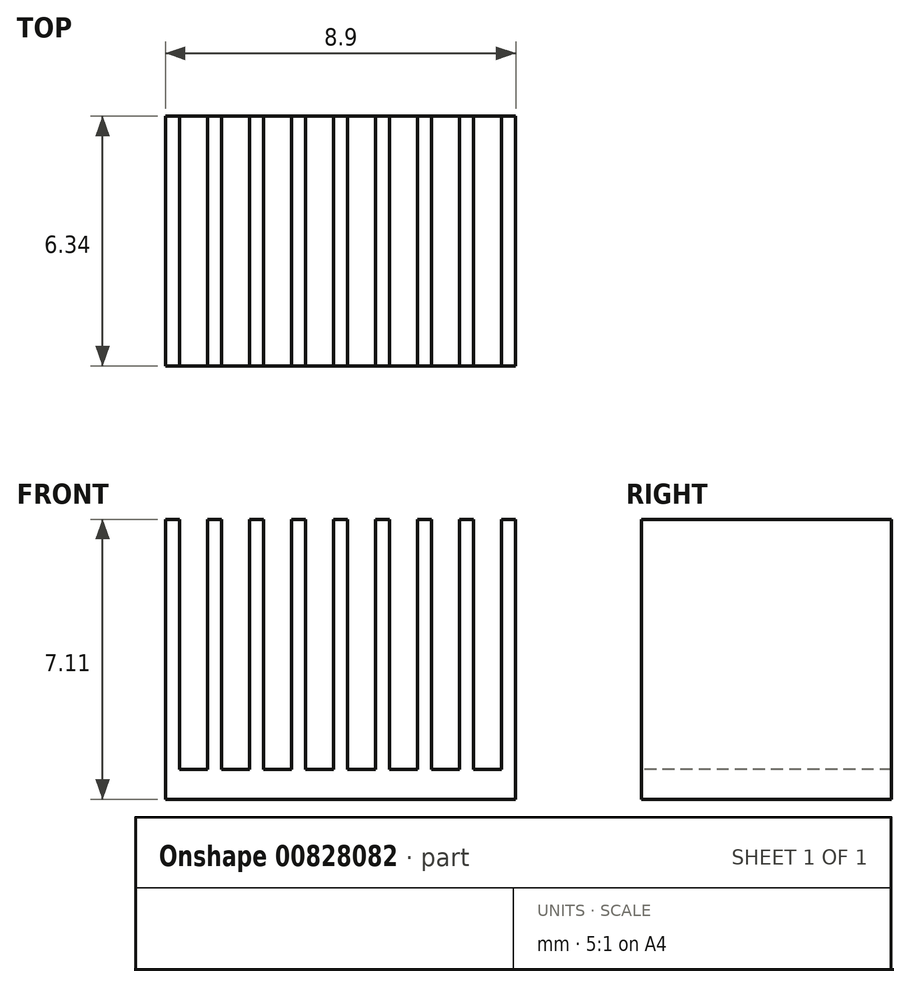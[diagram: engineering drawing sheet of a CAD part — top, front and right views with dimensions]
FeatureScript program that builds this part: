
annotation { "Feature Type Name" : "Feature", "Feature Type Description" : "" }
export const myFeature = defineFeature(function(context is Context, id is Id, definition is map)
    precondition{}
    {
        {
            var Q0;
            Q0=qCreatedBy(makeId("Top.planeOp"),FACE);
            var sketch = newSketch(context, id + "F0", { "sketchPlane" : qUnion([Q0])});
            skLineSegment(sketch, "E0.bottom", {"start": v(4.44, 3.18) * mm, "end": v(-4.45, 3.18) * mm});
            skLineSegment(sketch, "E0.top", {"start": v(4.45, -3.17) * mm, "end": v(-4.44, -3.17) * mm});
            skLineSegment(sketch, "E0.left", {"start": v(4.44, 3.18) * mm, "end": v(4.45, -3.17) * mm});
            skLineSegment(sketch, "E0.right", {"start": v(-4.45, 3.18) * mm, "end": v(-4.44, -3.17) * mm});
            skPoint(sketch, "E0.middle", {"position": v(0, 0) * mm});
            skSolve(sketch);
        }
        {
            var Q0;
            Q0=makeQuery(id+"F0.imprint","IMPRINT",FACE,{"disambiguationData":[TD([[makeQuery(id+"F0.imprint","IMPRINT",EDGE,{"derivedFrom":sQuery(id+"F0.wireOp",EDGE,"E0.bottom")}),1.0]])]});
            extrude(context, id + "F1", {"entities" : qUnion([Q0]), "depth" : 0.76 * mm, "offsetDistance" : 25.4 * mm});
        }
        {
            var Q0;
            Q0=makeQuery(id+"F1.opExtrude","CAP_FACE",FACE,{"disambiguationData":[OSD([sQuery(id+"F0.wireOp",EDGE,"E0.bottom"),sQuery(id+"F0.wireOp",EDGE,"E0.top"),sQuery(id+"F0.wireOp",EDGE,"E0.left"),sQuery(id+"F0.wireOp",EDGE,"E0.right")])],"isStart":false});
            var sketch = newSketch(context, id + "F2", { "sketchPlane" : qUnion([Q0])});
            skLineSegment(sketch, "E1.bottom", {"start": v(-4.45, 3.18) * mm, "end": v(-4.09, 3.18) * mm});
            skLineSegment(sketch, "E1.top", {"start": v(-4.45, -3.17) * mm, "end": v(-4.09, -3.17) * mm});
            skLineSegment(sketch, "E1.left", {"start": v(-4.45, 3.18) * mm, "end": v(-4.45, -3.17) * mm});
            skLineSegment(sketch, "E1.right", {"start": v(-4.09, 3.18) * mm, "end": v(-4.09, -3.17) * mm});
            skLineSegment(sketch, "E2.1.0.0", {"start": v(-3.02, 3.18) * mm, "end": v(-3.02, -3.17) * mm});
            skLineSegment(sketch, "E2.1.0.1", {"start": v(-3.38, 3.18) * mm, "end": v(-3.02, 3.18) * mm});
            skLineSegment(sketch, "E2.1.0.2", {"start": v(-3.38, 3.18) * mm, "end": v(-3.38, -3.17) * mm});
            skLineSegment(sketch, "E2.1.0.3", {"start": v(-3.38, -3.17) * mm, "end": v(-3.02, -3.17) * mm});
            skLineSegment(sketch, "E2.2.0.0", {"start": v(-1.96, 3.18) * mm, "end": v(-1.96, -3.17) * mm});
            skLineSegment(sketch, "E2.2.0.1", {"start": v(-2.31, 3.18) * mm, "end": v(-1.96, 3.18) * mm});
            skLineSegment(sketch, "E2.2.0.2", {"start": v(-2.31, 3.18) * mm, "end": v(-2.31, -3.17) * mm});
            skLineSegment(sketch, "E2.2.0.3", {"start": v(-2.31, -3.17) * mm, "end": v(-1.96, -3.17) * mm});
            skLineSegment(sketch, "E2.3.0.0", {"start": v(-0.89, 3.18) * mm, "end": v(-0.89, -3.17) * mm});
            skLineSegment(sketch, "E2.3.0.1", {"start": v(-1.24, 3.18) * mm, "end": v(-0.89, 3.18) * mm});
            skLineSegment(sketch, "E2.3.0.2", {"start": v(-1.24, 3.18) * mm, "end": v(-1.24, -3.17) * mm});
            skLineSegment(sketch, "E2.3.0.3", {"start": v(-1.24, -3.17) * mm, "end": v(-0.89, -3.17) * mm});
            skLineSegment(sketch, "E2.4.0.0", {"start": v(0.18, 3.18) * mm, "end": v(0.18, -3.17) * mm});
            skLineSegment(sketch, "E2.4.0.1", {"start": v(-0.18, 3.18) * mm, "end": v(0.18, 3.18) * mm});
            skLineSegment(sketch, "E2.4.0.2", {"start": v(-0.18, 3.18) * mm, "end": v(-0.18, -3.17) * mm});
            skLineSegment(sketch, "E2.4.0.3", {"start": v(-0.18, -3.17) * mm, "end": v(0.18, -3.17) * mm});
            skLineSegment(sketch, "E2.5.0.0", {"start": v(1.24, 3.18) * mm, "end": v(1.24, -3.17) * mm});
            skLineSegment(sketch, "E2.5.0.1", {"start": v(0.89, 3.18) * mm, "end": v(1.24, 3.18) * mm});
            skLineSegment(sketch, "E2.5.0.2", {"start": v(0.89, 3.18) * mm, "end": v(0.89, -3.17) * mm});
            skLineSegment(sketch, "E2.5.0.3", {"start": v(0.89, -3.17) * mm, "end": v(1.24, -3.17) * mm});
            skLineSegment(sketch, "E2.6.0.0", {"start": v(2.31, 3.18) * mm, "end": v(2.31, -3.17) * mm});
            skLineSegment(sketch, "E2.6.0.1", {"start": v(1.96, 3.18) * mm, "end": v(2.31, 3.18) * mm});
            skLineSegment(sketch, "E2.6.0.2", {"start": v(1.96, 3.18) * mm, "end": v(1.96, -3.17) * mm});
            skLineSegment(sketch, "E2.6.0.3", {"start": v(1.96, -3.17) * mm, "end": v(2.31, -3.17) * mm});
            skLineSegment(sketch, "E2.7.0.0", {"start": v(3.38, 3.18) * mm, "end": v(3.38, -3.17) * mm});
            skLineSegment(sketch, "E2.7.0.1", {"start": v(3.02, 3.18) * mm, "end": v(3.38, 3.18) * mm});
            skLineSegment(sketch, "E2.7.0.2", {"start": v(3.02, 3.18) * mm, "end": v(3.02, -3.17) * mm});
            skLineSegment(sketch, "E2.7.0.3", {"start": v(3.02, -3.17) * mm, "end": v(3.38, -3.17) * mm});
            skLineSegment(sketch, "E2.8.0.0", {"start": v(4.44, 3.18) * mm, "end": v(4.44, -3.17) * mm});
            skLineSegment(sketch, "E2.8.0.1", {"start": v(4.09, 3.18) * mm, "end": v(4.44, 3.18) * mm});
            skLineSegment(sketch, "E2.8.0.2", {"start": v(4.09, 3.18) * mm, "end": v(4.09, -3.17) * mm});
            skLineSegment(sketch, "E2.8.0.3", {"start": v(4.09, -3.17) * mm, "end": v(4.44, -3.17) * mm});
            skLineSegment(sketch, "E2.direction1", {"start": v(-4.09, -3.17) * mm, "end": v(-3.02, -3.17) * mm, "construction": true});
            skSolve(sketch);
        }
        {
            var Q0;
            Q0=makeQuery(id+"F2.imprint","IMPRINT",FACE,{"disambiguationData":[TD([[makeQuery(id+"F2.imprint","IMPRINT",EDGE,{"derivedFrom":sQuery(id+"F2.wireOp",EDGE,"E1.bottom")}),1.0]])]});
            var Q1;
            Q1=makeQuery(id+"F2.imprint","IMPRINT",FACE,{"disambiguationData":[TD([[makeQuery(id+"F2.imprint","IMPRINT",EDGE,{"derivedFrom":sQuery(id+"F2.wireOp",EDGE,"E2.1.0.0")}),-1.0]])]});
            var Q2;
            Q2=makeQuery(id+"F2.imprint","IMPRINT",FACE,{"disambiguationData":[TD([[makeQuery(id+"F2.imprint","IMPRINT",EDGE,{"derivedFrom":sQuery(id+"F2.wireOp",EDGE,"E2.2.0.0")}),-1.0]])]});
            var Q3;
            Q3=makeQuery(id+"F2.imprint","IMPRINT",FACE,{"disambiguationData":[TD([[makeQuery(id+"F2.imprint","IMPRINT",EDGE,{"derivedFrom":sQuery(id+"F2.wireOp",EDGE,"E2.3.0.0")}),-1.0]])]});
            var Q4;
            Q4=makeQuery(id+"F2.imprint","IMPRINT",FACE,{"disambiguationData":[TD([[makeQuery(id+"F2.imprint","IMPRINT",EDGE,{"derivedFrom":sQuery(id+"F2.wireOp",EDGE,"E2.4.0.0")}),-1.0]])]});
            var Q5;
            Q5=makeQuery(id+"F2.imprint","IMPRINT",FACE,{"disambiguationData":[TD([[makeQuery(id+"F2.imprint","IMPRINT",EDGE,{"derivedFrom":sQuery(id+"F2.wireOp",EDGE,"E2.5.0.0")}),-1.0]])]});
            var Q6;
            Q6=makeQuery(id+"F2.imprint","IMPRINT",FACE,{"disambiguationData":[TD([[makeQuery(id+"F2.imprint","IMPRINT",EDGE,{"derivedFrom":sQuery(id+"F2.wireOp",EDGE,"E2.6.0.0")}),-1.0]])]});
            var Q7;
            Q7=makeQuery(id+"F2.imprint","IMPRINT",FACE,{"disambiguationData":[TD([[makeQuery(id+"F2.imprint","IMPRINT",EDGE,{"derivedFrom":sQuery(id+"F2.wireOp",EDGE,"E2.7.0.0")}),-1.0]])]});
            var Q8;
            Q8=makeQuery(id+"F2.imprint","IMPRINT",FACE,{"disambiguationData":[TD([[makeQuery(id+"F2.imprint","IMPRINT",EDGE,{"derivedFrom":sQuery(id+"F2.wireOp",EDGE,"E2.8.0.0")}),-1.0]])]});
            extrude(context, id + "F3", {"entities" : qUnion([Q0, Q1, Q2, Q3, Q4, Q5, Q6, Q7, Q8]), "operationType" : NewBodyOperationType.ADD, "depth" : 6.35 * mm, "offsetDistance" : 25.4 * mm});
        }
    });
